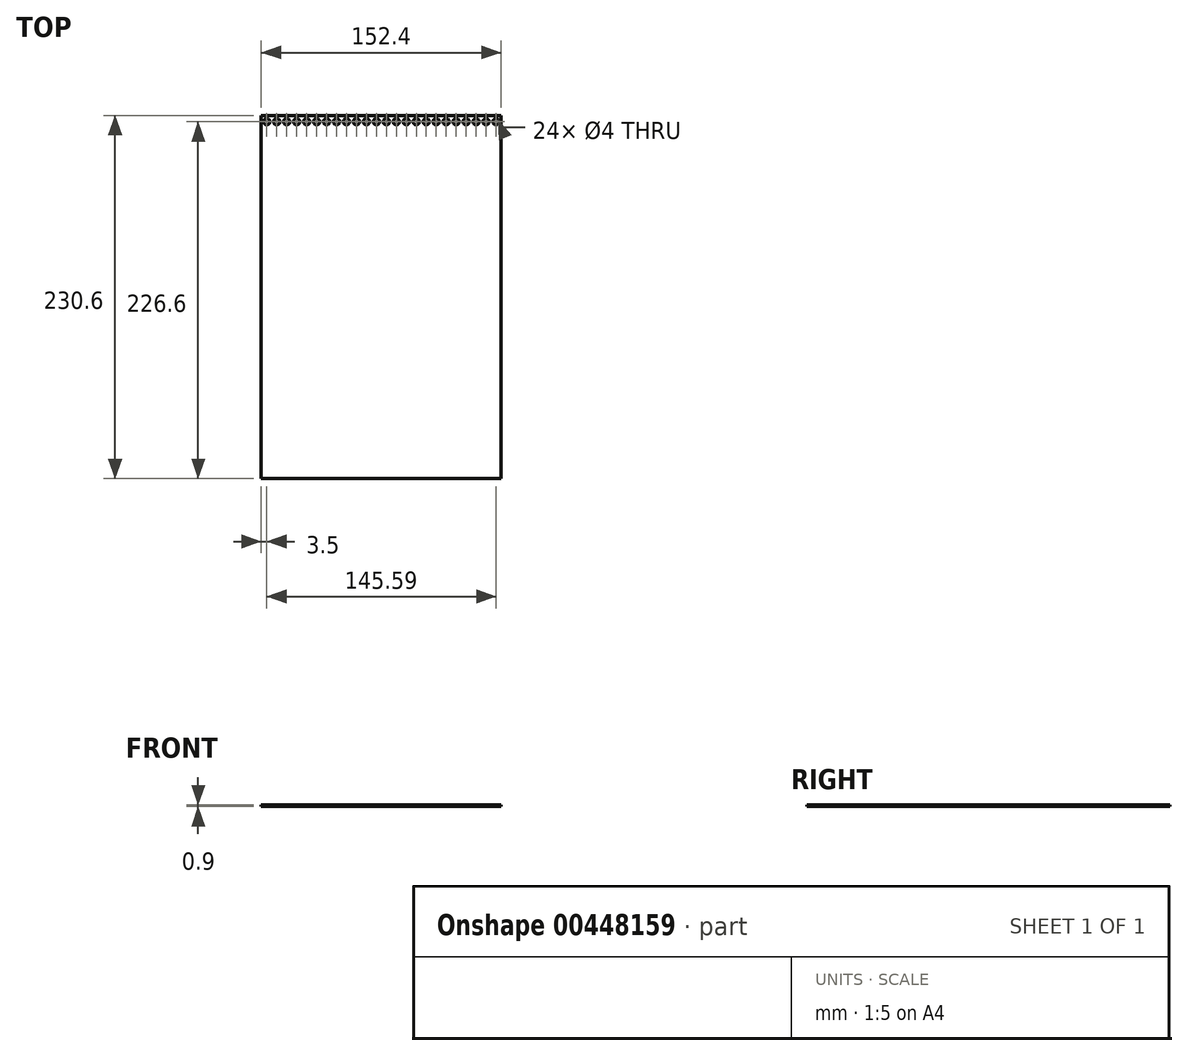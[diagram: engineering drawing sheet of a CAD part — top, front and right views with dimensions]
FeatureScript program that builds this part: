
annotation { "Feature Type Name" : "Feature", "Feature Type Description" : "" }
export const myFeature = defineFeature(function(context is Context, id is Id, definition is map)
    precondition{}
    {
        {
            var Q0;
            Q0=qCreatedBy(makeId("Top.planeOp"),FACE);
            var sketch = newSketch(context, id + "F0", { "sketchPlane" : qUnion([Q0])});
            skLineSegment(sketch, "E0.bottom", {"start": v(152.4, 0) * mm, "end": v(0, 0) * mm});
            skLineSegment(sketch, "E0.top", {"start": v(152.4, 230.6) * mm, "end": v(0, 230.6) * mm});
            skLineSegment(sketch, "E0.left", {"start": v(152.4, 0) * mm, "end": v(152.4, 230.6) * mm});
            skLineSegment(sketch, "E0.right", {"start": v(0, 0) * mm, "end": v(0, 230.6) * mm});
            skPoint(sketch, "E0.middle", {"position": v(76.2, 115.3) * mm});
            skCircle(sketch, "E1", {"center": v(3.5, 226.6) * mm, "radius": 2 * mm});
            skCircle(sketch, "E2.1.0.0", {"center": v(9.83, 226.6) * mm, "radius": 2 * mm});
            skCircle(sketch, "E2.2.0.0", {"center": v(16.16, 226.6) * mm, "radius": 2 * mm});
            skCircle(sketch, "E2.3.0.0", {"center": v(22.49, 226.6) * mm, "radius": 2 * mm});
            skCircle(sketch, "E2.4.0.0", {"center": v(28.82, 226.6) * mm, "radius": 2 * mm});
            skCircle(sketch, "E2.5.0.0", {"center": v(35.15, 226.6) * mm, "radius": 2 * mm});
            skCircle(sketch, "E2.6.0.0", {"center": v(41.48, 226.6) * mm, "radius": 2 * mm});
            skCircle(sketch, "E2.7.0.0", {"center": v(47.81, 226.6) * mm, "radius": 2 * mm});
            skCircle(sketch, "E2.8.0.0", {"center": v(54.14, 226.6) * mm, "radius": 2 * mm});
            skCircle(sketch, "E2.9.0.0", {"center": v(60.47, 226.6) * mm, "radius": 2 * mm});
            skCircle(sketch, "E2.10.0.0", {"center": v(66.8, 226.6) * mm, "radius": 2 * mm});
            skCircle(sketch, "E2.11.0.0", {"center": v(73.13, 226.6) * mm, "radius": 2 * mm});
            skCircle(sketch, "E2.12.0.0", {"center": v(79.46, 226.6) * mm, "radius": 2 * mm});
            skCircle(sketch, "E2.13.0.0", {"center": v(85.8, 226.6) * mm, "radius": 2 * mm});
            skCircle(sketch, "E2.14.0.0", {"center": v(92.12, 226.6) * mm, "radius": 2 * mm});
            skCircle(sketch, "E2.15.0.0", {"center": v(98.45, 226.6) * mm, "radius": 2 * mm});
            skCircle(sketch, "E2.16.0.0", {"center": v(104.78, 226.6) * mm, "radius": 2 * mm});
            skCircle(sketch, "E2.17.0.0", {"center": v(111.11, 226.6) * mm, "radius": 2 * mm});
            skCircle(sketch, "E2.18.0.0", {"center": v(117.44, 226.6) * mm, "radius": 2 * mm});
            skCircle(sketch, "E2.19.0.0", {"center": v(123.77, 226.6) * mm, "radius": 2 * mm});
            skCircle(sketch, "E2.20.0.0", {"center": v(130.1, 226.6) * mm, "radius": 2 * mm});
            skCircle(sketch, "E2.21.0.0", {"center": v(136.43, 226.6) * mm, "radius": 2 * mm});
            skCircle(sketch, "E2.22.0.0", {"center": v(142.76, 226.6) * mm, "radius": 2 * mm});
            skCircle(sketch, "E2.23.0.0", {"center": v(149.1, 226.6) * mm, "radius": 2 * mm});
            skLineSegment(sketch, "E2.direction1", {"start": v(3.5, 226.6) * mm, "end": v(9.83, 226.6) * mm, "construction": true});
            skLineSegment(sketch, "E3", {"start": v(3.5, 230.6) * mm, "end": v(3.5, 0) * mm, "construction": true});
            skSolve(sketch);
        }
        {
            var Q0;
            Q0=makeQuery(id+"F0.imprint","IMPRINT",FACE,{"disambiguationData":[TD([[makeQuery(id+"F0.imprint","IMPRINT",EDGE,{"derivedFrom":sQuery(id+"F0.wireOp",EDGE,"xspdwd4T-hh9s-YhL0-CR4h-a1rttdloaoXV.bottom")}),-1.0]])]});
            var Q1;
            Q1=makeQuery(id+"F0.imprint","IMPRINT",FACE,{"disambiguationData":[TD([[makeQuery(id+"F0.imprint","IMPRINT",EDGE,{"derivedFrom":sQuery(id+"F0.wireOp",EDGE,"EyKOLEKs-VKrM-iXOC-hHu5-3qqzj1gGHgoQ.top")}),-1.0]])]});
            var Q2;
            Q2=makeQuery(id+"F0.imprint","IMPRINT",FACE,{"disambiguationData":[TD([[makeQuery(id+"F0.imprint","IMPRINT",EDGE,{"derivedFrom":sQuery(id+"F0.wireOp",EDGE,"E0.bottom")}),-1.0]])]});
            extrude(context, id + "F1", {"entities" : qUnion([Q0, Q1, Q2]), "depth" : .9 * mm});
        }
    });
